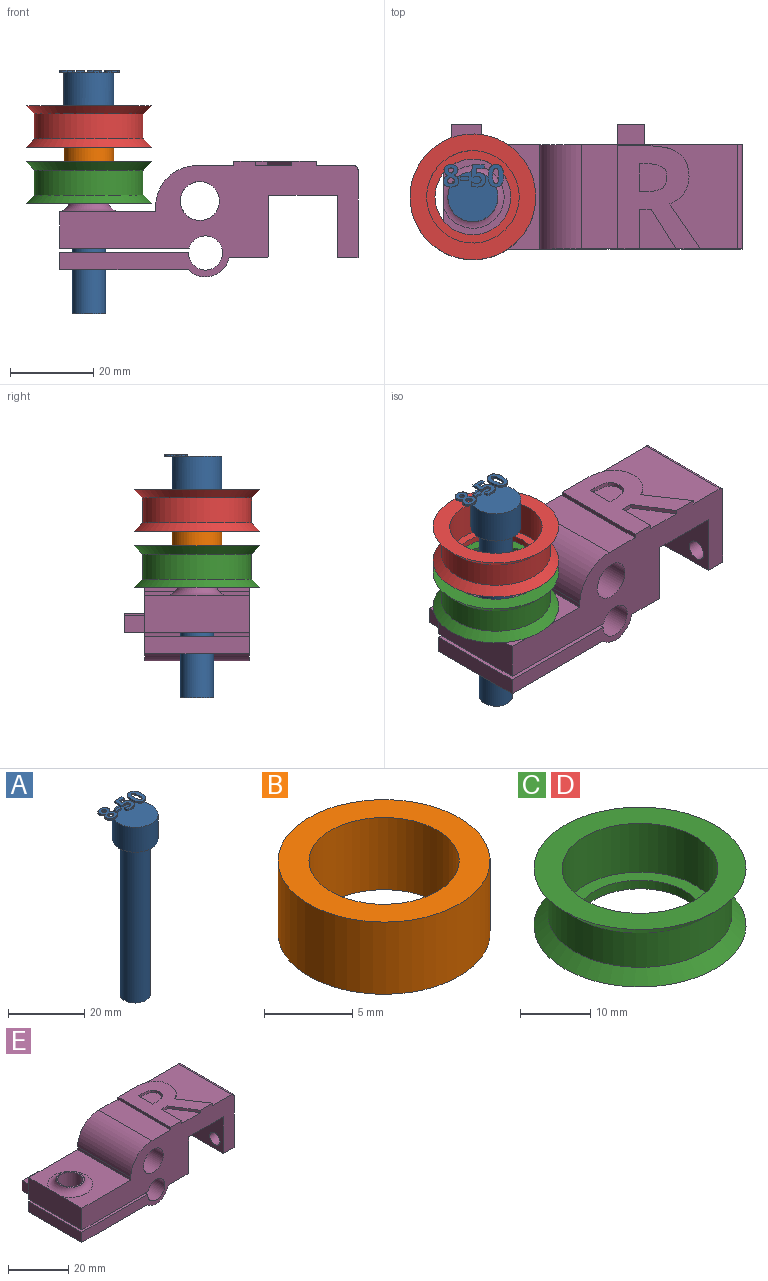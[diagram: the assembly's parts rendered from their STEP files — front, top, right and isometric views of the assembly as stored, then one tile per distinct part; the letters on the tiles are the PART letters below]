
ASSEMBLY  parts=5 mates=4
PART A: 86 faces, bbox 14.5x13.7x58.5 mm
  f0: plane 12x12mm, normal (0,0,1), area 99.4mm2, adj f5,f22,f23,f24,f25,f26,f40,f41
  f1: plane 1x0.26mm, normal (0,0,1), area 0.1mm2, adj f5,f46,f47,f48,f49
  f2: plane 0.85x0.68mm, normal (0,0,1), area 0.2mm2, adj f5,f29,f30,f31
  f3: cylinder r=4mm len=50mm, axis (0,0,-1), area 1256.6mm2, adj f4,f6
  f4: plane 8x8mm, normal (0,0,-1), area 50.3mm2, adj f3
  f5: cylinder r=6mm len=12mm, axis (0,0,-1), area 301.6mm2, adj f0,f1,f2,f6,f39,f45,f67,f85
  f6: plane 12x12mm, normal (0,0,-1), area 62.8mm2, adj f3,f5
  f7: extruded ~0.5x0.46mm, area 0.2mm2, adj f8,f37,f38,f39
  f8: extruded ~0.5x0.46mm, area 0.2mm2, adj f7,f9,f38,f39
  f9: extruded ~0.5x0.39mm, area 0.2mm2, adj f8,f10,f38,f39
  f10: extruded ~0.5x0.4mm, area 0.2mm2, adj f9,f11,f38,f39
  f11: extruded ~0.5x0.49mm, area 0.3mm2, adj f10,f12,f38,f39
  f12: extruded ~0.5x0.5mm, area 0.3mm2, adj f11,f13,f38,f39
  f13: extruded ~0.5x0.39mm, area 0.2mm2, adj f12,f37,f38,f39
  f14: extruded ~1.22x0.5mm, area 0.6mm2, adj f15,f35,f38,f39
  f15: extruded ~1.22x0.5mm, area 0.6mm2, adj f14,f16,f38,f39
  f16: extruded ~0.91x0.5mm, area 0.5mm2, adj f15,f17,f38,f39
  f17: extruded ~0.71x0.5mm, area 0.4mm2, adj f16,f18,f38,f39
  f18: extruded ~0.65x0.61mm, area 0.4mm2, adj f17,f19,f38,f39
  f19: extruded ~0.77x0.62mm, area 0.5mm2, adj f18,f20,f38,f39
  f20: extruded ~0.8x0.5mm, area 0.4mm2, adj f19,f21,f38,f39
  f21: extruded ~1.04x0.5mm, area 0.6mm2, adj f20,f22,f38,f39
  f22: extruded ~1.36x0.5mm, area 0.7mm2, adj f0,f21,f23,f38,f39
  f23: extruded ~1.33x0.5mm, area 0.7mm2, adj f0,f22,f24,f38
  f24: extruded ~1.04x0.51mm, area 0.6mm2, adj f0,f23,f25,f38
  f25: extruded ~0.75x0.5mm, area 0.4mm2, adj f0,f24,f26,f38
  f26: extruded ~0.85x0.66mm, area 0.5mm2, adj f0,f25,f27,f38,f39
  f27: extruded ~0.72x0.56mm, area 0.5mm2, adj f26,f28,f38,f39
  f28: extruded ~0.72x0.5mm, area 0.4mm2, adj f27,f35,f38,f39
  f29: extruded ~0.5x0.45mm, area 0.3mm2, adj f2,f30,f36,f38,f39
  f30: extruded ~0.5x0.47mm, area 0.3mm2, adj f2,f29,f31,f38
  f31: extruded ~0.62x0.5mm, area 0.3mm2, adj f2,f30,f32,f38,f39
  f32: extruded ~0.59x0.5mm, area 0.3mm2, adj f31,f33,f38,f39
  f33: extruded ~0.5x0.48mm, area 0.3mm2, adj f32,f34,f38,f39
  f34: extruded ~0.89x0.77mm, area 0.6mm2, adj f33,f36,f38,f39
  f35: extruded ~0.93x0.5mm, area 0.5mm2, adj f14,f28,f38,f39
  f36: extruded ~0.66x0.5mm, area 0.4mm2, adj f29,f34,f38,f39
  f37: extruded ~0.5x0.39mm, area 0.2mm2, adj f7,f13,f38,f39
  f38: plane 5.4x3.69mm, normal (0,0,1), area 12.7mm2, adj f7,f8,f9,f10,f11,f12,f13,f14
  f39: plane 5.4x3.53mm, normal (0,0,-1), area 10.2mm2, adj f5,f7,f8,f9,f10,f11,f12,f13
  f40: plane 0.9x0.5mm, normal (-1,0,0), area 0.4mm2, adj f0,f41,f43,f44
  f41: plane 1.93x0.5mm, normal (0,-1,0), area 1mm2, adj f0,f40,f42,f44
  f42: plane 0.9x0.5mm, normal (1,0,0), area 0.4mm2, adj f0,f41,f43,f44
  f43: plane 1.93x0.5mm, normal (0,1,0), area 1mm2, adj f0,f40,f42,f44
  f44: plane 1.93x0.9mm, normal (0,0,1), area 1.7mm2, adj f40,f41,f42,f43
  f45: plane 0.76x0.31mm, normal (0,0,-1), area 0mm2, adj f5,f46
  f46: extruded ~1.21x0.5mm, area 0.7mm2, adj f0,f1,f45,f47,f65,f66
  f47: extruded ~0.54x0.5mm, area 0.3mm2, adj f1,f46,f48,f66
  f48: plane 0.5x0.13mm, normal (-0.2,0.98,0), area 0.1mm2, adj f1,f47,f49,f66
  f49: plane 1.03x0.5mm, normal (1,-0.09,0), area 0.5mm2, adj f1,f48,f50,f66,f67
  f50: plane 1.88x0.5mm, normal (0,-1,0), area 0.9mm2, adj f49,f51,f66,f67
  f51: plane 0.94x0.5mm, normal (1,0,0), area 0.5mm2, adj f50,f52,f66,f67
  f52: plane 2.85x0.5mm, normal (0,1,0), area 1.4mm2, adj f51,f53,f66,f67
  f53: plane 2.68x0.5mm, normal (-1,0.07,0), area 1.3mm2, adj f0,f52,f54,f66,f67
  f54: plane 0.5x0.44mm, normal (-0.47,-0.88,0), area 0.3mm2, adj f0,f53,f55,f66
  f55: extruded ~0.5x0.37mm, area 0.2mm2, adj f0,f54,f56,f66
  f56: extruded ~0.5x0.42mm, area 0.2mm2, adj f0,f55,f57,f66
  f57: extruded ~1.05x0.8mm, area 0.8mm2, adj f0,f56,f58,f66
  f58: extruded ~1.02x0.83mm, area 0.8mm2, adj f0,f57,f59,f66
  f59: extruded ~0.72x0.5mm, area 0.4mm2, adj f0,f58,f60,f66
  f60: extruded ~0.66x0.5mm, area 0.4mm2, adj f0,f59,f61,f66
  f61: plane 0.96x0.5mm, normal (-1,0,0), area 0.5mm2, adj f0,f60,f62,f66
  f62: extruded ~1.42x0.5mm, area 0.7mm2, adj f0,f61,f63,f66
  f63: extruded ~1.55x0.5mm, area 0.8mm2, adj f0,f62,f64,f66
  f64: extruded ~1.36x0.54mm, area 0.8mm2, adj f0,f63,f65,f66
  f65: extruded ~1.17x0.5mm, area 0.6mm2, adj f0,f46,f64,f66
  f66: plane 5.33x3.51mm, normal (0,0,1), area 10.9mm2, adj f46,f47,f48,f49,f50,f51,f52,f53
  f67: plane 2.97x1.71mm, normal (0,0,-1), area 3.5mm2, adj f5,f49,f50,f51,f52,f53
  f68: extruded ~1.39x0.5mm, area 0.7mm2, adj f69,f83,f84,f85
  f69: extruded ~1.39x0.5mm, area 0.7mm2, adj f68,f70,f84,f85
  f70: extruded ~0.56x0.5mm, area 0.4mm2, adj f69,f71,f84,f85
  f71: extruded ~0.56x0.5mm, area 0.4mm2, adj f70,f72,f84,f85
  f72: extruded ~1.39x0.5mm, area 0.7mm2, adj f71,f73,f84,f85
  f73: extruded ~1.38x0.5mm, area 0.7mm2, adj f72,f74,f84,f85
  f74: extruded ~0.56x0.5mm, area 0.4mm2, adj f73,f83,f84,f85
  f75: extruded ~2.04x0.5mm, area 1.1mm2, adj f76,f82,f84,f85
  f76: extruded ~2.02x0.5mm, area 1.1mm2, adj f75,f77,f84,f85
  f77: extruded ~1.38x0.69mm, area 0.8mm2, adj f76,f78,f84,f85
  f78: extruded ~1.38x0.66mm, area 0.8mm2, adj f77,f79,f84,f85
  f79: extruded ~2.05x0.5mm, area 1.1mm2, adj f78,f80,f84,f85
  f80: extruded ~2.02x0.5mm, area 1mm2, adj f0,f79,f81,f84,f85
  f81: extruded ~1.37x0.68mm, area 0.8mm2, adj f0,f80,f82,f84
  f82: extruded ~1.39x0.66mm, area 0.8mm2, adj f0,f75,f81,f84,f85
  f83: extruded ~0.56x0.5mm, area 0.4mm2, adj f68,f74,f84,f85
  f84: plane 5.41x3.68mm, normal (0,0,1), area 12.1mm2, adj f68,f69,f70,f71,f72,f73,f74,f75
  f85: plane 5.41x3.68mm, normal (0,0,-1), area 10.3mm2, adj f5,f68,f69,f70,f71,f72,f73,f74
PART B: 4 faces, bbox 12x12x5 mm
  f0: cylinder r=4.25mm len=8.5mm, axis (0,0,-1), area 133.5mm2, adj f2,f3
  f1: cylinder r=6mm len=12mm, axis (0,0,-1), area 188.5mm2, adj f2,f3
  f2: plane 12x12mm, normal (0,0,1), area 56.4mm2, adj f0,f1
  f3: plane 12x12mm, normal (0,0,-1), area 56.4mm2, adj f0,f1
PART C: 8 faces, bbox 30.2x30.2x10 mm
  f0: plane 30.2x30.2mm, normal (0,0,1), area 329.2mm2, adj f1,f7
  f1: cylinder r=11.1mm len=22.2mm, axis (0,0,-1), area 592.8mm2, adj f0,f2
  f2: plane 22.2x22.2mm, normal (0,0,1), area 126.9mm2, adj f1,f3
  f3: cylinder r=9.1mm len=18.2mm, axis (0,0,-1), area 85.8mm2, adj f2,f4
  f4: plane 30.2x30.2mm, normal (0,0,-1), area 456.2mm2, adj f3,f5
  f5: cone r=13.1mm half-angle=45deg, axis (0,0,-1), area 250.6mm2, adj f4,f6
  f6: cylinder r=13.1mm len=26.2mm, axis (0,0,-1), area 493.9mm2, adj f5,f7
  f7: cone r=15.1mm half-angle=45deg, axis (0,0,1), area 250.6mm2, adj f0,f6
PART D: same geometry as C
PART E: 56 faces, bbox 75.1x30x27.7 mm
  f0: plane 37.62x25mm, normal (0,0,1), area 547.1mm2, adj f14,f15,f25,f27,f40,f41,f42,f43
  f1: plane 9.51x8.71mm, normal (0,0,1), area 54.7mm2, adj f14,f37,f38,f39
  f2: plane 25x4.12mm, normal (-1,0,0), area 103mm2, adj f5,f14,f15,f19
  f3: cylinder r=4.17mm len=8.35mm, axis (0,0,1), area 108.1mm2, adj f5,f19
  f4: plane 25x9.34mm, normal (0,0,-1), area 233.4mm2, adj f13,f14,f15,f17
  f5: plane 30.88x25mm, normal (0,0,-1), area 717.2mm2, adj f2,f3,f14,f15,f17
  f6: plane 25x8.82mm, normal (-1,0,0), area 219.6mm2, adj f7,f14,f15,f20,f24
  f7: plane 25x23mm, normal (0,0,1), area 400mm2, adj f6,f8,f14,f15,f24
  f8: plane 25x1.1mm, normal (-1,0,0), area 27.5mm2, adj f7,f14,f15,f25
  f9: plane 25x21.09mm, normal (1,0,0), area 493.5mm2, adj f10,f14,f15,f22,f23,f27
  f10: plane 25x5mm, normal (0,0,-1), area 125mm2, adj f9,f11,f14,f15
  f11: plane 25x15mm, normal (-1,0,0), area 341.3mm2, adj f10,f12,f14,f15,f22,f23
  f12: plane 25x16.4mm, normal (0,0,-1), area 410mm2, adj f11,f13,f14,f15
  f13: plane 25x14.91mm, normal (1,0,-0.01), area 372.8mm2, adj f4,f12,f14,f15
  f14: plane 71.62x27.75mm, normal (0,-1,0), area 1041.8mm2, adj f0,f1,f2,f4,f5,f6,f7,f8
  f15: plane 71.62x26.75mm, normal (0,1,0), area 970.7mm2, adj f0,f2,f4,f5,f6,f7,f8,f9
  f16: cylinder r=4.17mm len=10.78mm, axis (0,0,1), area 282.8mm2, adj f20,f21
  f17: cylinder r=5.75mm len=25mm, axis (0,-1,0), area 315.9mm2, adj f4,f5,f14,f15
  f18: cylinder r=4.1mm len=25mm, axis (0,-1,0), area 618.7mm2, adj f14,f15,f19,f20
  f19: plane 30.91x25mm, normal (0,0,1), area 718.1mm2, adj f2,f3,f14,f15,f18
  f20: plane 31.07x30mm, normal (0,0,-1), area 758.4mm2, adj f6,f14,f15,f16,f18,f29,f30,f31
  f21: plane 9.35x9.35mm, normal (0,0,1), area 13.9mm2, adj f16,f24
  f22: cylinder r=2.43mm len=5mm, axis (1,0,0), area 76.2mm2, adj f9,f11
  f23: cylinder r=2.2mm len=5mm, axis (1,0,0), area 69.1mm2, adj f9,f11
  f24: torus R=7.5mm, axis (0,0,-1), area 134.6mm2, adj f6,f7,f21
  f25: cylinder r=10mm len=25mm, axis (0,-1,0), area 392.7mm2, adj f0,f8,f14,f15
  f26: cylinder r=4.68mm len=25mm, axis (0,-1,0), area 735.2mm2, adj f14,f15
  f27: cylinder r=1mm len=25mm, axis (0,-1,0), area 39.3mm2, adj f0,f9,f14,f15
  f28: plane 7.3x5mm, normal (0,0,1), area 36.5mm2, adj f15,f29,f30,f31
  f29: plane 5x4.12mm, normal (-1,0,0), area 20.6mm2, adj f15,f20,f28,f31
  f30: plane 5x4.12mm, normal (1,0,0), area 20.6mm2, adj f15,f20,f28,f31
  f31: plane 7.3x4.12mm, normal (0,1,0), area 30.1mm2, adj f20,f28,f29,f30
  f32: plane 6.63x5mm, normal (0,0,1), area 33.2mm2, adj f15,f33,f35,f36
  f33: plane 5x4.5mm, normal (-1,0,0), area 22.5mm2, adj f15,f32,f34,f36
  f34: plane 6.63x5mm, normal (0,0,-1), area 33.2mm2, adj f15,f33,f35,f36
  f35: plane 5x4.5mm, normal (1,0,0), area 22.5mm2, adj f15,f32,f34,f36
  f36: plane 6.63x4.5mm, normal (0,1,0), area 29.9mm2, adj f32,f33,f34,f35
  f37: plane 9.51x1mm, normal (1,0,0), area 9.5mm2, adj f1,f14,f38,f54
  f38: plane 2.79x1mm, normal (0,-1,0), area 2.8mm2, adj f1,f37,f39,f54
  f39: plane 9.51x5.92mm, normal (-0.85,-0.53,0), area 11.2mm2, adj f1,f14,f38,f54
  f40: extruded ~10.8x7.29mm, area 13mm2, adj f0,f14,f41,f54
  f41: extruded ~3.41x2.67mm, area 4.4mm2, adj f0,f40,f42,f54
  f42: extruded ~3.89x1.2mm, area 4.1mm2, adj f0,f41,f43,f54
  f43: extruded ~5.59x2.42mm, area 6.3mm2, adj f0,f42,f44,f54
  f44: extruded ~7.48x1.84mm, area 7.8mm2, adj f0,f43,f45,f54
  f45: plane 7.22x1mm, normal (0,1,0), area 7.2mm2, adj f0,f44,f46,f54
  f46: plane 24.79x1mm, normal (-1,0,0), area 24.8mm2, adj f0,f14,f45,f54
  f47: plane 1.69x1mm, normal (0,1,0), area 1.7mm2, adj f48,f53,f54,f55
  f48: plane 6.7x1mm, normal (1,0,0), area 6.7mm2, adj f47,f49,f54,f55
  f49: plane 1.6x1mm, normal (0,-1,0), area 1.6mm2, adj f48,f50,f54,f55
  f50: extruded ~3.75x1mm, area 3.9mm2, adj f49,f51,f54,f55
  f51: extruded ~2.51x1.21mm, area 2.9mm2, adj f50,f52,f54,f55
  f52: extruded ~2.61x1.19mm, area 3mm2, adj f51,f53,f54,f55
  f53: extruded ~3.68x1mm, area 3.8mm2, adj f47,f52,f54,f55
  f54: plane 24.79x19.8mm, normal (0,0,1), area 300mm2, adj f14,f37,f38,f39,f40,f41,f42,f43
  f55: plane 6.7x6.56mm, normal (0,0,1), area 38.8mm2, adj f47,f48,f49,f50,f51,f52,f53
PLACE A t=(-103.78,-12.5,-13.6)mm
PLACE B rot(axis=(1,0,0),180deg) t=(-103.78,-12.5,26.4)mm
PLACE C t=(-103.78,-12.5,18.1)mm
PLACE D t=(-103.78,-12.5,31.6)mm
PLACE E at identity
MATE fastened A.f3 <-> D.f1  axis (0,0,-1) through (-103.78,-12.5,36.4)mm
MATE fastened B.f0 <-> C.f1  axis (0,0,1) through (-103.78,-12.5,21.4)mm
MATE fastened C.f1 <-> E.f3  axis (0,0,-1) through (-103.78,-12.5,12.9)mm
MATE fastened D.f1 <-> B.f0  axis (0,0,-1) through (-103.78,-12.5,26.4)mm
